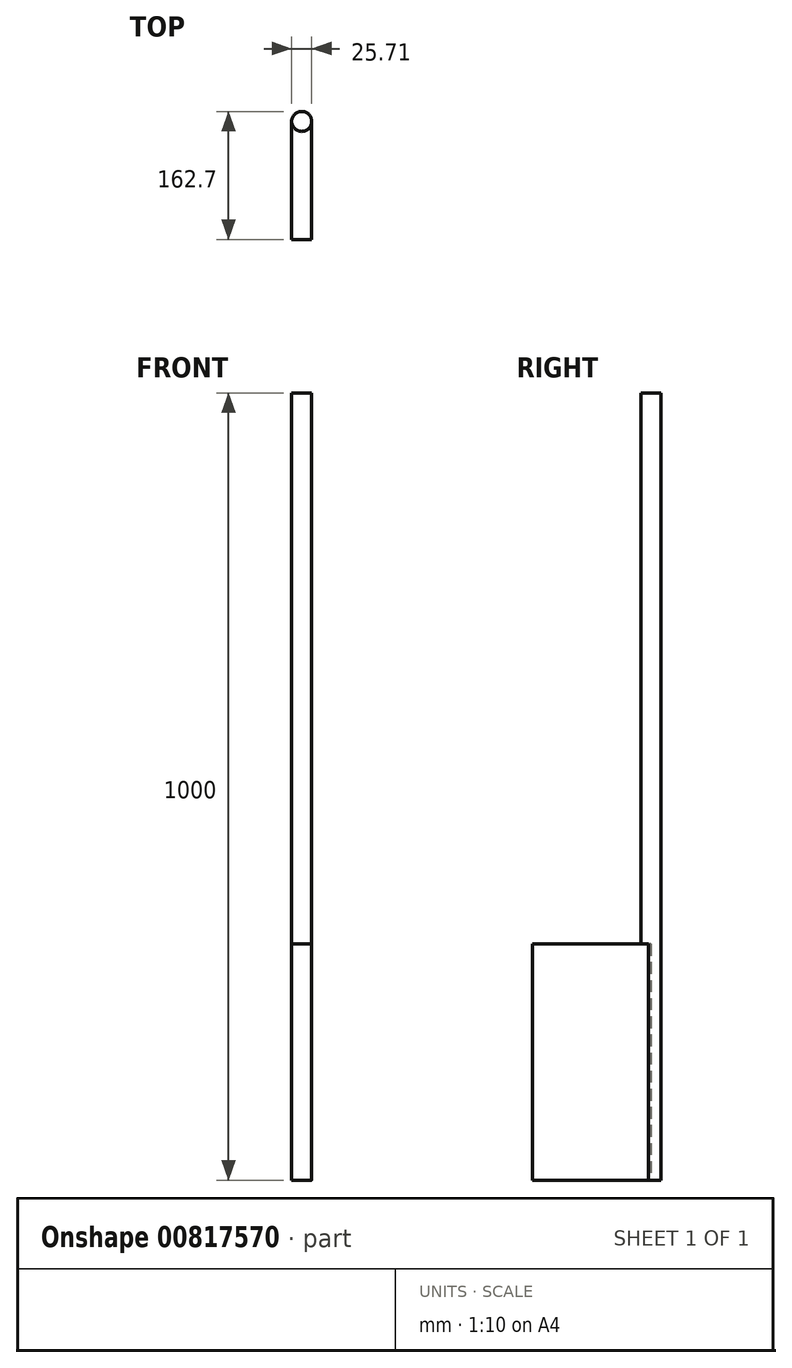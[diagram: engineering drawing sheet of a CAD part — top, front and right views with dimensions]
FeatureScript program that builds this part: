
annotation { "Feature Type Name" : "Feature", "Feature Type Description" : "" }
export const myFeature = defineFeature(function(context is Context, id is Id, definition is map)
    precondition{}
    {
        {
            var Q0;
            Q0=qCreatedBy(makeId("Top.planeOp"),FACE);
            var sketch = newSketch(context, id + "F0", { "sketchPlane" : qUnion([Q0])});
            skCircle(sketch, "E0", {"center": v(0, 0) * mm, "radius": 12.7 * mm});
            skSolve(sketch);
        }
        {
            var Q0;
            Q0=makeQuery(id+"F0.imprint","IMPRINT",FACE,{"disambiguationData":[TD([[makeQuery(id+"F0.imprint","IMPRINT",EDGE,{"derivedFrom":sQuery(id+"F0.wireOp",EDGE,"E0")}),1.0]])]});
            extrude(context, id + "F1", {"entities" : qUnion([Q0]), "depth" : 1000 * mm, "offsetDistance" : 25.4 * mm});
        }
        {
            var Q0;
            Q0=qCreatedBy(makeId("Front.planeOp"),FACE);
            var sketch = newSketch(context, id + "F2", { "sketchPlane" : qUnion([Q0])});
            skLineSegment(sketch, "E1.bottom", {"start": v(-13.01, 0) * mm, "end": v(12.39, 0) * mm});
            skLineSegment(sketch, "E1.top", {"start": v(-13.01, 300) * mm, "end": v(12.39, 300) * mm});
            skLineSegment(sketch, "E1.left", {"start": v(-13.01, 0) * mm, "end": v(-13.01, 300) * mm});
            skLineSegment(sketch, "E1.right", {"start": v(12.39, 0) * mm, "end": v(12.39, 300) * mm});
            skSolve(sketch);
        }
        {
            var Q0;
            Q0 = qSketchRegion(id + "F2", true);
            extrude(context, id + "F3", {"entities" : qUnion([Q0]), "operationType" : NewBodyOperationType.ADD, "depth" : 150 * mm, "offsetDistance" : 25.4 * mm});
        }
    });
